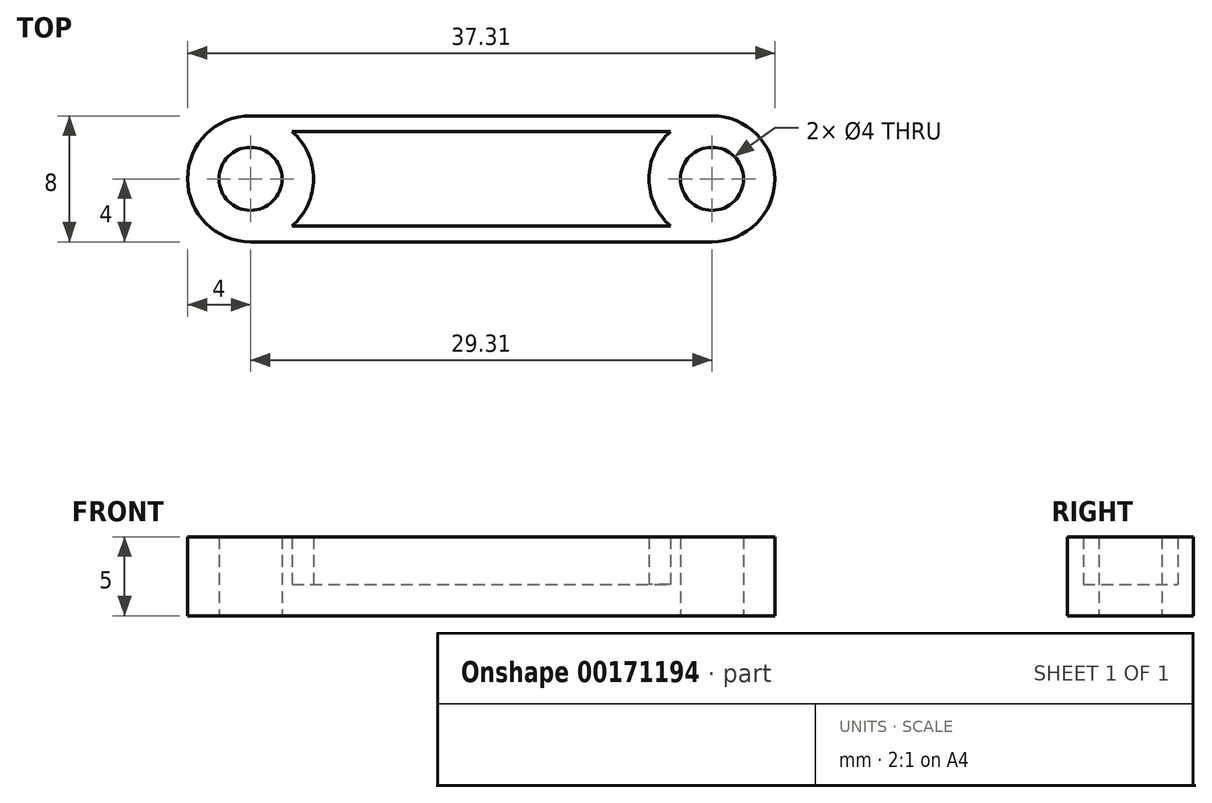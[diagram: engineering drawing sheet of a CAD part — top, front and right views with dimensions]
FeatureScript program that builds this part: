
annotation { "Feature Type Name" : "Feature", "Feature Type Description" : "" }
export const myFeature = defineFeature(function(context is Context, id is Id, definition is map)
    precondition{}
    {
        {
            var Q0;
            Q0=qCreatedBy(makeId("Top.planeOp"),FACE);
            var sketch = newSketch(context, id + "F0", { "sketchPlane" : qUnion([Q0])});
            skLineSegment(sketch, "E0", {"start": v(0, 0) * mm, "end": v(29.3, 0) * mm, "construction": true});
            skCircle(sketch, "E1", {"center": v(0, 0) * mm, "radius": 2 * mm});
            skCircle(sketch, "E2", {"center": v(0, 0) * mm, "radius": 4 * mm});
            skCircle(sketch, "E3", {"center": v(29.3, 0) * mm, "radius": 2 * mm});
            skCircle(sketch, "E4", {"center": v(29.3, 0) * mm, "radius": 4 * mm});
            skLineSegment(sketch, "E5", {"start": v(0, 4) * mm, "end": v(29.3, 4) * mm});
            skLineSegment(sketch, "E6", {"start": v(0, -4) * mm, "end": v(29.3, -4) * mm});
            skCircle(sketch, "E7", {"center": v(0, 0) * mm, "radius": 3 * mm, "construction": true});
            skCircle(sketch, "E8", {"center": v(29.3, 0) * mm, "radius": 3 * mm, "construction": true});
            skLineSegment(sketch, "E9", {"start": v(0, 3) * mm, "end": v(29.3, 3) * mm, "construction": true});
            skLineSegment(sketch, "E10", {"start": v(0, -3) * mm, "end": v(29.3, -3) * mm, "construction": true});
            skLineSegment(sketch, "E11", {"start": v(2.65, 3) * mm, "end": v(26.66, 3) * mm});
            skLineSegment(sketch, "E12", {"start": v(2.65, -3) * mm, "end": v(26.66, -3) * mm});
            skSolve(sketch);
        }
        {
            var Q0;
            Q0=makeQuery(id+"F0.imprint","IMPRINT",FACE,{"disambiguationData":[TD([[makeQuery(id+"F0.imprint","IMPRINT",EDGE,{"derivedFrom":sQuery(id+"F0.wireOp",EDGE,"E1")}),-1.0]])]});
            var Q1;
            {var subQ0=sQuery(id+"F0.wireOp",EDGE,"E5");Q1=makeQuery(id+"F0.imprint","IMPRINT",FACE,{"disambiguationData":[TD([[makeQuery(id+"F0.imprint","IMPRINT",EDGE,{"derivedFrom":subQ0}),-1.0]])]});}
            var Q2;
            {var subQ0=sQuery(id+"F0.wireOp",EDGE,"E6");Q2=makeQuery(id+"F0.imprint","IMPRINT",FACE,{"disambiguationData":[TD([[makeQuery(id+"F0.imprint","IMPRINT",EDGE,{"derivedFrom":subQ0}),1.0]])]});}
            var Q3;
            Q3=makeQuery(id+"F0.imprint","IMPRINT",FACE,{"disambiguationData":[TD([[makeQuery(id+"F0.imprint","IMPRINT",EDGE,{"derivedFrom":sQuery(id+"F0.wireOp",EDGE,"E3")}),-1.0]])]});
            extrude(context, id + "F1", {"entities" : qUnion([Q0, Q1, Q2, Q3]), "depth" : 5 * mm});
        }
        {
            var Q0;
            Q0 = qSketchRegion(id + "F0", true);
            var Q1;
            {var subQ0=sQuery(id+"F0.wireOp",EDGE,"E11");Q1=makeQuery(id+"F0.imprint","IMPRINT",FACE,{"disambiguationData":[TD([[makeQuery(id+"F0.imprint","IMPRINT",EDGE,{"derivedFrom":subQ0}),-1.0]])]});}
            extrude(context, id + "F2", {"entities" : qUnion([Q0, Q1]), "operationType" : NewBodyOperationType.ADD, "depth" : 2 * mm});
        }
    });
